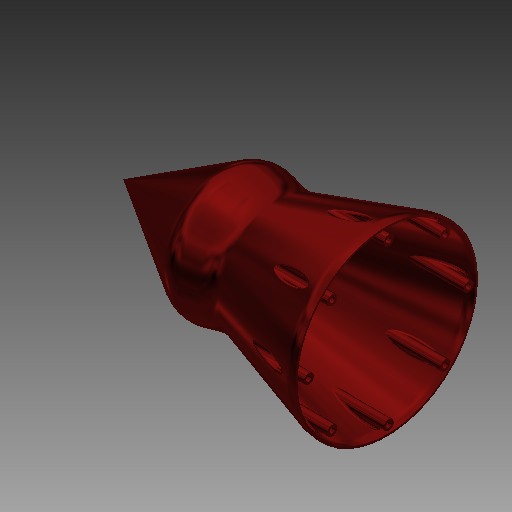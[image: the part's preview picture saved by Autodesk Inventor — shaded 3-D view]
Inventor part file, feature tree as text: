
AUTODESK INVENTOR PART (.ipt)
format: ipt  version: 2019 (Build 230136000, 136)  size: 819,200 bytes
history: native  units: in
note: dims shown in document units (in); Inventor stores cm internally (conversion verified against a paired STEP export)
features: sketch x3, plane x2, fillet x2, revolve x1, extrude x1, other x1, hole x1, pattern_circular x1
ambient origin geometry x8: Origin, YZ Plane, XZ Plane, XY Plane, X Axis, Y Axis, Z Axis, Center Point
bodies: Solid1 (feature_tree)
feature tree (12):
  revolve  "Revolution1"  [1 undecoded]
  plane  "Work Plane2"
  extrude  "Extrusion4"  Depth=3.937in
  plane  "Work Plane4"
  sketch  "Sketch10"  dims[d26=0.1168in d27=0.1181in d31=0.0787in d33=90.0deg d51=0.0787in d66=0.3937in d67=0.0in d68=-0.3937in d94=0.3937in d95=0.3937in d71=0.2047in d72=0.2362in d73=0.3543in d74=0.1969in d75=90.0deg d76=0.315in d77=0.8108in d80=0.0787in d81=0.0787in d85=3.1496in d86=360.0deg d88=0.3937in d89=3.0709in d90=0.9449in d91=1.5748in d92=3.4252in d93=0.9055in d78=0.0394in d79=0.0394in]
  other  "Work Point1"
  hole  "Hole1"  [1 undecoded]
  fillet  "Fillet2"  Radius=0.0787in
  fillet  "Fillet3"  [1 undecoded]
  pattern_circular  "Circular Pattern2"  [2 undecoded]
  sketch  "Sketch3"  dims[d11=4.4488in d17=0.6299in]
  sketch  "Sketch8"  dims[d19=30.0deg d24=3.937in]
note: 5 required parameter values undecoded (feature->parameter linkage not recoverable at this tier; creation-order binding heuristic only, values carry confidence <= 0.55)